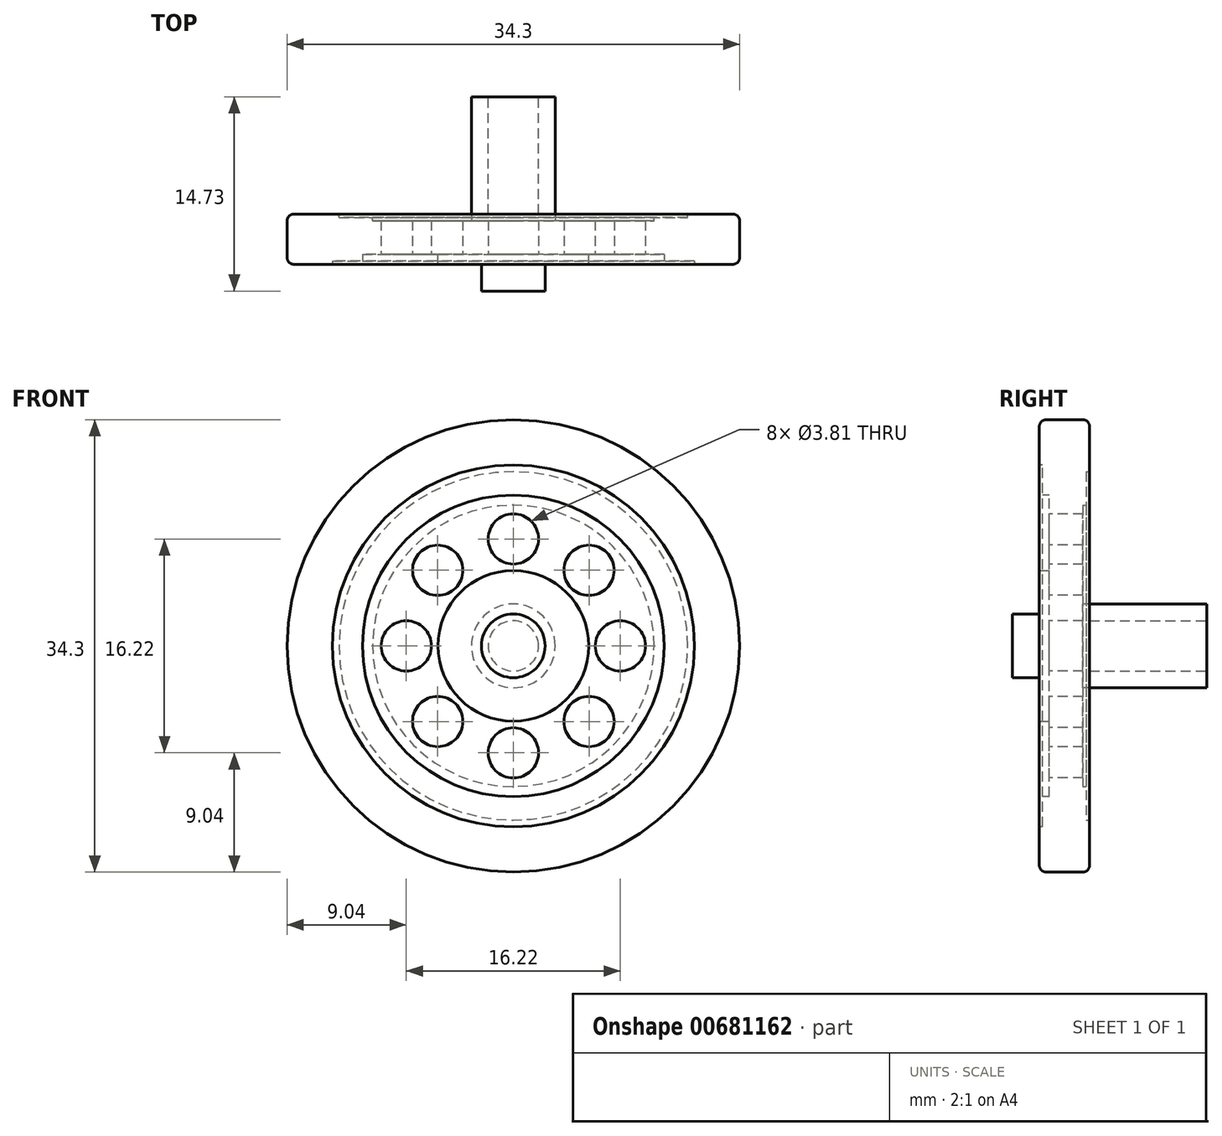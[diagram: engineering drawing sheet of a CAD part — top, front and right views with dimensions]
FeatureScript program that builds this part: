
annotation { "Feature Type Name" : "Feature", "Feature Type Description" : "" }
export const myFeature = defineFeature(function(context is Context, id is Id, definition is map)
    precondition{}
    {
        {
            var Q0;
            Q0=qCreatedBy(makeId("Front.planeOp"),FACE);
            var sketch = newSketch(context, id + "F0", { "sketchPlane" : qUnion([Q0])});
            skCircle(sketch, "E0", {"center": v(0, 0) * mm, "radius": 17.15 * mm});
            skSolve(sketch);
        }
        {
            var Q0;
            Q0 = qSketchRegion(id + "F0", true);
            extrude(context, id + "F1", {"entities" : qUnion([Q0]), "depth" : 3.8 * mm, "offsetDistance" : 25.4 * mm});
        }
        {
            var Q0;
            Q0=makeQuery(id+"F1.opExtrude","CAP_FACE",FACE,{"disambiguationData":[OSD([sQuery(id+"F0.wireOp",EDGE,"E0")])],"isStart":false});
            var sketch = newSketch(context, id + "F2", { "sketchPlane" : qUnion([Q0])});
            skCircle(sketch, "E1", {"center": v(0, 0) * mm, "radius": 13.72 * mm});
            skCircle(sketch, "E2", {"center": v(0, 0) * mm, "radius": 11.43 * mm});
            skSolve(sketch);
        }
        {
            var Q0;
            Q0=makeQuery(id+"F2.imprint","IMPRINT",FACE,{"disambiguationData":[TD([[makeQuery(id+"F2.imprint","IMPRINT",EDGE,{"derivedFrom":sQuery(id+"F2.wireOp",EDGE,"E1")}),1.0]])]});
            extrude(context, id + "F3", {"entities" : qUnion([Q0]), "operationType" : NewBodyOperationType.REMOVE, "oppositeDirection" : true, "depth" : 0.25 * mm, "offsetDistance" : 25.4 * mm});
        }
        {
            var Q0;
            Q0=makeQuery(id+"F3.boolean.opBoolean","SPLIT",FACE,{"disambiguationData":[TD([makeQuery(id+"F3.opExtrude","SWEPT_FACE",FACE,{"disambiguationData":[OSD([sQuery(id+"F2.wireOp",EDGE,"E2")])]})])],"derivedFrom":makeQuery(id+"F1.opExtrude","CAP_FACE",FACE,{"disambiguationData":[OSD([sQuery(id+"F0.wireOp",EDGE,"E0")])],"isStart":false})});
            extrude(context, id + "F4", {"entities" : qUnion([Q0]), "operationType" : NewBodyOperationType.REMOVE, "oppositeDirection" : true, "depth" : 0.76 * mm, "offsetDistance" : 25.4 * mm});
        }
        {
            var Q0;
            Q0=makeQuery(id+"F4.boolean.opBoolean","COPY",FACE,{"derivedFrom":makeQuery(id+"F4.opExtrude","CAP_FACE",FACE,{"disambiguationData":[OSD([sQuery(id+"F0.wireOp",EDGE,"E0")])],"isStart":false})});
            var sketch = newSketch(context, id + "F5", { "sketchPlane" : qUnion([Q0])});
            skCircle(sketch, "E3", {"center": v(0, 0) * mm, "radius": 5.71 * mm});
            skSolve(sketch);
        }
        {
            var Q0;
            Q0=makeQuery(id+"F5.imprint","IMPRINT",FACE,{"disambiguationData":[TD([[makeQuery(id+"F5.imprint","IMPRINT",EDGE,{"derivedFrom":sQuery(id+"F5.wireOp",EDGE,"E3")}),1.0]])]});
            extrude(context, id + "F6", {"entities" : qUnion([Q0]), "operationType" : NewBodyOperationType.ADD, "depth" : 0.76 * mm, "offsetDistance" : 25.4 * mm});
        }
        {
            var Q0;
            Q0=makeQuery(id+"F6.opExtrude","CAP_FACE",FACE,{"disambiguationData":[OSD([sQuery(id+"F5.wireOp",EDGE,"E3")])],"isStart":false});
            var sketch = newSketch(context, id + "F7", { "sketchPlane" : qUnion([Q0])});
            skCircle(sketch, "E4", {"center": v(0, 0) * mm, "radius": 2.41 * mm});
            skSolve(sketch);
        }
        {
            var Q0;
            Q0=makeQuery(id+"F4.boolean.opBoolean","COPY",FACE,{"derivedFrom":makeQuery(id+"F4.opExtrude","CAP_FACE",FACE,{"disambiguationData":[OSD([sQuery(id+"F0.wireOp",EDGE,"E0")])],"isStart":false})});
            var sketch = newSketch(context, id + "F8", { "sketchPlane" : qUnion([Q0])});
            skCircle(sketch, "E5", {"center": v(0, 8.11) * mm, "radius": 1.9 * mm});
            skCircle(sketch, "E6.1.0", {"center": v(-5.73, 5.73) * mm, "radius": 1.9 * mm});
            skCircle(sketch, "E6.2.0", {"center": v(-8.11, 0) * mm, "radius": 1.9 * mm});
            skCircle(sketch, "E6.3.0", {"center": v(-5.73, -5.73) * mm, "radius": 1.9 * mm});
            skCircle(sketch, "E6.4.0", {"center": v(0, -8.11) * mm, "radius": 1.9 * mm});
            skCircle(sketch, "E6.5.0", {"center": v(5.73, -5.73) * mm, "radius": 1.9 * mm});
            skCircle(sketch, "E6.6.0", {"center": v(8.11, 0) * mm, "radius": 1.9 * mm});
            skCircle(sketch, "E6.7.0", {"center": v(5.73, 5.73) * mm, "radius": 1.9 * mm});
            skPoint(sketch, "E6.center", {"position": v(0, 0) * mm});
            skSolve(sketch);
        }
        {
            var Q0;
            Q0=makeQuery(id+"F8.imprint","IMPRINT",FACE,{"disambiguationData":[TD([[makeQuery(id+"F8.imprint","IMPRINT",EDGE,{"derivedFrom":sQuery(id+"F8.wireOp",EDGE,"E5")}),1.0]])]});
            var Q1;
            Q1=makeQuery(id+"F8.imprint","IMPRINT",FACE,{"disambiguationData":[TD([[makeQuery(id+"F8.imprint","IMPRINT",EDGE,{"derivedFrom":sQuery(id+"F8.wireOp",EDGE,"E6.1.0")}),1.0]])]});
            var Q2;
            Q2=makeQuery(id+"F8.imprint","IMPRINT",FACE,{"disambiguationData":[TD([[makeQuery(id+"F8.imprint","IMPRINT",EDGE,{"derivedFrom":sQuery(id+"F8.wireOp",EDGE,"E6.3.0")}),1.0]])]});
            var Q3;
            Q3=makeQuery(id+"F8.imprint","IMPRINT",FACE,{"disambiguationData":[TD([[makeQuery(id+"F8.imprint","IMPRINT",EDGE,{"derivedFrom":sQuery(id+"F8.wireOp",EDGE,"E6.4.0")}),1.0]])]});
            var Q4;
            Q4=makeQuery(id+"F8.imprint","IMPRINT",FACE,{"disambiguationData":[TD([[makeQuery(id+"F8.imprint","IMPRINT",EDGE,{"derivedFrom":sQuery(id+"F8.wireOp",EDGE,"E6.5.0")}),1.0]])]});
            var Q5;
            Q5=makeQuery(id+"F8.imprint","IMPRINT",FACE,{"disambiguationData":[TD([[makeQuery(id+"F8.imprint","IMPRINT",EDGE,{"derivedFrom":sQuery(id+"F8.wireOp",EDGE,"E6.6.0")}),1.0]])]});
            var Q6;
            Q6=makeQuery(id+"F8.imprint","IMPRINT",FACE,{"disambiguationData":[TD([[makeQuery(id+"F8.imprint","IMPRINT",EDGE,{"derivedFrom":sQuery(id+"F8.wireOp",EDGE,"E6.7.0")}),1.0]])]});
            var Q7;
            Q7=makeQuery(id+"F8.imprint","IMPRINT",FACE,{"disambiguationData":[TD([[makeQuery(id+"F8.imprint","IMPRINT",EDGE,{"derivedFrom":sQuery(id+"F8.wireOp",EDGE,"E6.2.0")}),1.0]])]});
            extrude(context, id + "F9", {"entities" : qUnion([Q0, Q1, Q2, Q3, Q4, Q5, Q6, Q7]), "operationType" : NewBodyOperationType.REMOVE, "oppositeDirection" : true, "depth" : 25.4 * mm, "offsetDistance" : 25.4 * mm});
        }
        {
            var Q0;
            Q0=makeQuery(id+"F7.imprint","IMPRINT",FACE,{"disambiguationData":[TD([[makeQuery(id+"F7.imprint","IMPRINT",EDGE,{"derivedFrom":sQuery(id+"F7.wireOp",EDGE,"E4")}),1.0]])]});
            var sketch = newSketch(context, id + "F10", { "sketchPlane" : qUnion([Q0])});
            skSolve(sketch);
        }
        {
            var Q0;
            Q0=makeQuery(id+"F10.imprint","IMPRINT",FACE,{"disambiguationData":[TD([[makeQuery(id+"F10.imprint","IMPRINT",EDGE,{"derivedFrom":makeQuery(id+"F7.imprint","IMPRINT",EDGE,{"derivedFrom":sQuery(id+"F7.wireOp",EDGE,"E4")})}),1.0]])]});
            extrude(context, id + "F11", {"entities" : qUnion([Q0]), "operationType" : NewBodyOperationType.ADD, "depth" : 2.03 * mm, "offsetDistance" : 25.4 * mm});
        }
        {
            var Q0;
            Q0=makeQuery(id+"F7.imprint","IMPRINT",FACE,{"disambiguationData":[TD([[makeQuery(id+"F7.imprint","IMPRINT",EDGE,{"derivedFrom":sQuery(id+"F7.wireOp",EDGE,"E4")}),-1.0]])]});
            var sketch = newSketch(context, id + "F12", { "sketchPlane" : qUnion([Q0])});
            skCircle(sketch, "E7", {"center": v(0, 4.32) * mm, "radius": 0.64 * mm});
            skCircle(sketch, "E8.1.0", {"center": v(-2.54, 3.5) * mm, "radius": 0.64 * mm});
            skCircle(sketch, "E8.2.0", {"center": v(-4.11, 1.34) * mm, "radius": 0.64 * mm});
            skCircle(sketch, "E8.3.0", {"center": v(-4.11, -1.34) * mm, "radius": 0.64 * mm});
            skCircle(sketch, "E8.4.0", {"center": v(-2.54, -3.5) * mm, "radius": 0.64 * mm});
            skCircle(sketch, "E8.5.0", {"center": v(0, -4.32) * mm, "radius": 0.64 * mm});
            skCircle(sketch, "E8.6.0", {"center": v(2.54, -3.5) * mm, "radius": 0.64 * mm});
            skCircle(sketch, "E8.7.0", {"center": v(4.11, -1.34) * mm, "radius": 0.64 * mm});
            skCircle(sketch, "E8.8.0", {"center": v(4.11, 1.34) * mm, "radius": 0.64 * mm});
            skCircle(sketch, "E8.9.0", {"center": v(2.54, 3.5) * mm, "radius": 0.64 * mm});
            skPoint(sketch, "E8.center", {"position": v(0, 0) * mm});
            skSolve(sketch);
        }
        {
            var Q0;
            Q0=sQuery(id+"F12.wireOp",EDGE,"E7");
            var Q1;
            Q1=sQuery(id+"F12.wireOp",EDGE,"E8.9.0");
            var Q2;
            Q2=sQuery(id+"F12.wireOp",EDGE,"E8.8.0");
            var Q3;
            Q3=sQuery(id+"F12.wireOp",EDGE,"E8.6.0");
            var Q4;
            Q4=sQuery(id+"F12.wireOp",EDGE,"E8.5.0");
            var Q5;
            Q5=sQuery(id+"F12.wireOp",EDGE,"E8.4.0");
            var Q6;
            Q6=sQuery(id+"F12.wireOp",EDGE,"E8.3.0");
            var Q7;
            Q7=sQuery(id+"F12.wireOp",EDGE,"E8.2.0");
            var Q8;
            Q8=sQuery(id+"F12.wireOp",EDGE,"E8.1.0");
            var Q9;
            Q9=sQuery(id+"F12.wireOp",EDGE,"E8.7.0");
            extrude(context, id + "F13", {"bodyType" : ToolBodyType.SURFACE, "surfaceEntities" : qUnion([Q0, Q1, Q2, Q3, Q4, Q5, Q6, Q7, Q8, Q9]), "depth" : 0.25 * mm, "offsetDistance" : 25.4 * mm});
        }
        {
            var Q0;
            Q0=qCreatedBy(makeId("Front.planeOp"),FACE);
            var sketch = newSketch(context, id + "F14", { "sketchPlane" : qUnion([Q0])});
            skCircle(sketch, "E9", {"center": v(0, 0) * mm, "radius": 3.18 * mm});
            skSolve(sketch);
        }
        {
            var Q0;
            Q0 = qSketchRegion(id + "F14", true);
            extrude(context, id + "F15", {"entities" : qUnion([Q0]), "operationType" : NewBodyOperationType.ADD, "oppositeDirection" : true, "depth" : 8.9 * mm, "offsetDistance" : 25.4 * mm});
        }
        {
            var Q0;
            Q0=makeQuery(id+"F15.opExtrude","CAP_FACE",FACE,{"disambiguationData":[OSD([sQuery(id+"F14.wireOp",EDGE,"E9")])],"isStart":false});
            var sketch = newSketch(context, id + "F16", { "sketchPlane" : qUnion([Q0])});
            skCircle(sketch, "E10", {"center": v(0, 0) * mm, "radius": 1.9 * mm});
            skSolve(sketch);
        }
        {
            var Q0;
            Q0=makeQuery(id+"F16.imprint","IMPRINT",FACE,{"disambiguationData":[TD([[makeQuery(id+"F16.imprint","IMPRINT",EDGE,{"derivedFrom":sQuery(id+"F16.wireOp",EDGE,"E10")}),1.0]])]});
            extrude(context, id + "F17", {"entities" : qUnion([Q0]), "operationType" : NewBodyOperationType.REMOVE, "oppositeDirection" : true, "depth" : 8.9 * mm, "offsetDistance" : 25.4 * mm});
        }
        {
            var Q0;
            Q0=makeQuery(id+"F1.opExtrude","CAP_EDGE",EDGE,{"disambiguationData":[OSD([sQuery(id+"F0.wireOp",EDGE,"E0")])],"isStart":false});
            fillet(context, id + "F18", {"entities" : qUnion([Q0]), "radius" : 0.5 * mm, "tangentPropagation" : true, "allowEdgeOverflow" : false});
        }
        {
            var Q0;
            Q0=makeQuery(id+"F1.opExtrude","CAP_EDGE",EDGE,{"disambiguationData":[OSD([sQuery(id+"F0.wireOp",EDGE,"E0")])],"isStart":true});
            fillet(context, id + "F19", {"entities" : qUnion([Q0]), "radius" : 0.5 * mm, "tangentPropagation" : true, "allowEdgeOverflow" : false});
        }
        {
            var Q0;
            Q0=makeQuery(id+"F1.opExtrude","CAP_FACE",FACE,{"disambiguationData":[OSD([sQuery(id+"F0.wireOp",EDGE,"E0")])],"isStart":true});
            var sketch = newSketch(context, id + "F20", { "sketchPlane" : qUnion([Q0])});
            skCircle(sketch, "E11", {"center": v(0, 0) * mm, "radius": 13.2 * mm});
            skCircle(sketch, "E12", {"center": v(0, 0) * mm, "radius": 10.67 * mm});
            skSolve(sketch);
        }
        {
            var Q0;
            Q0 = qSketchRegion(id + "F20", true);
            extrude(context, id + "F21", {"entities" : qUnion([Q0]), "operationType" : NewBodyOperationType.REMOVE, "oppositeDirection" : true, "depth" : 0.25 * mm, "offsetDistance" : 25.4 * mm});
        }
        {
            var Q0;
            Q0=makeQuery(id+"F21.boolean.opBoolean","SPLIT",FACE,{"disambiguationData":[TD([makeQuery(id+"F9.boolean.opBoolean","COPY",FACE,{"derivedFrom":makeQuery(id+"F9.opExtrude","SWEPT_FACE",FACE,{"disambiguationData":[OSD([sQuery(id+"F8.wireOp",EDGE,"E5")])]})})])],"derivedFrom":makeQuery(id+"F1.opExtrude","CAP_FACE",FACE,{"disambiguationData":[OSD([sQuery(id+"F0.wireOp",EDGE,"E0")])],"isStart":true})});
            extrude(context, id + "F22", {"entities" : qUnion([Q0]), "operationType" : NewBodyOperationType.REMOVE, "oppositeDirection" : true, "depth" : 0.5 * mm, "offsetDistance" : 25.4 * mm});
        }
    });
